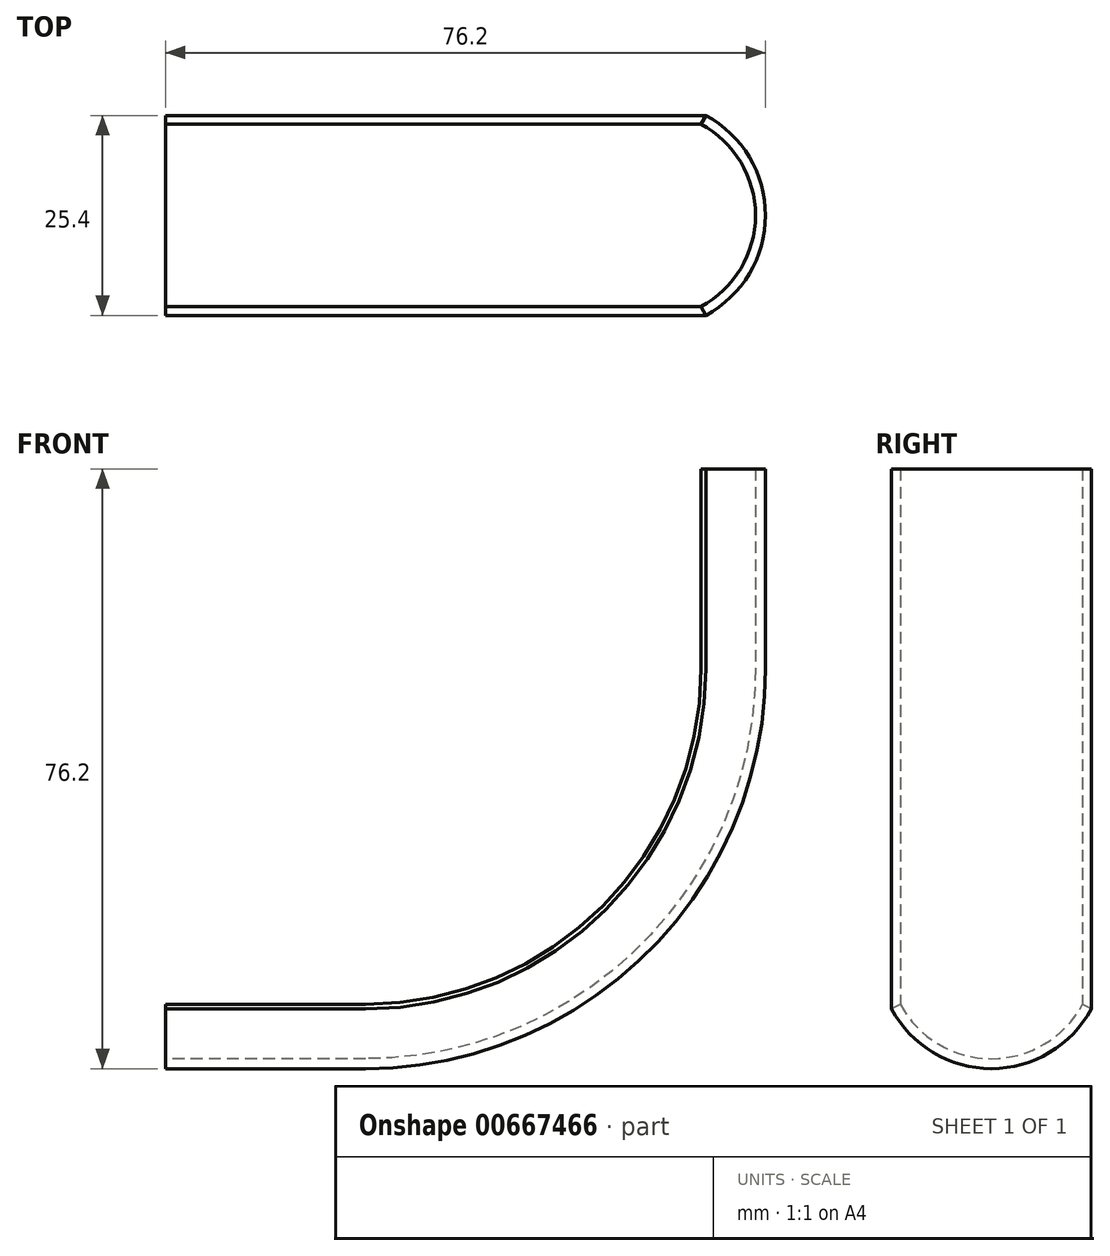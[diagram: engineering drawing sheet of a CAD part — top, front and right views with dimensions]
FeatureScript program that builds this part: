
annotation { "Feature Type Name" : "Feature", "Feature Type Description" : "" }
export const myFeature = defineFeature(function(context is Context, id is Id, definition is map)
    precondition{}
    {
        {
            var Q0;
            Q0=qCreatedBy(makeId("Front.planeOp"),FACE);
            var sketch = newSketch(context, id + "F0", { "sketchPlane" : qUnion([Q0])});
            skLineSegment(sketch, "E0", {"start": v(-76.2, 0) * mm, "end": v(-50.8, 0) * mm});
            skArc(sketch, "E1", {"start": v(-50.8, 0) * mm, "mid": v(-14.88, 14.88) * mm, "end": v(0, 50.8) * mm});
            skLineSegment(sketch, "E2", {"start": v(0, 50.8) * mm, "end": v(0, 76.2) * mm});
            skSolve(sketch);
        }
        {
            var Q0;
            Q0=qCreatedBy(makeId("Right.planeOp"),FACE);
            cPlane(context, id + "F1", {"entities" : qUnion([Q0]), "cplaneType" : CPlaneType.OFFSET, "offset" : 50.8 * mm, "oppositeDirection" : true, "width" : 152.4 * mm, "height" : 152.4 * mm});
        }
        {
            var Q0;
            Q0=qCreatedBy(id+"F1.planeOp",FACE);
            var sketch = newSketch(context, id + "F2", { "sketchPlane" : qUnion([Q0])});
            skArc(sketch, "E3", {"start": v(-12.7, 7.59) * mm, "mid": v(0, 0) * mm, "end": v(12.7, 7.59) * mm});
            skArc(sketch, "E4.0", {"start": v(-11.58, 8.2) * mm, "mid": v(0, 1.27) * mm, "end": v(11.58, 8.2) * mm});
            skLineSegment(sketch, "E5", {"start": v(12.7, 7.59) * mm, "end": v(11.58, 8.2) * mm});
            skLineSegment(sketch, "E6", {"start": v(-11.58, 8.2) * mm, "end": v(-12.7, 7.59) * mm});
            skSolve(sketch);
        }
        {
            var Q0;
            Q0 = qSketchRegion(id + "F2", true);
            var Q1;
            Q1 = qConstructionFilter(qBodyType(qCreatedBy(id + "F0" ,EDGE), BodyType.WIRE), ConstructionObject.NO);
            sweep(context, id + "F3", {"profiles" : qUnion([Q0]), "path" : qUnion([Q1])});
        }
    });
